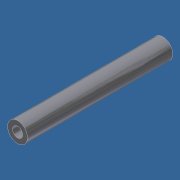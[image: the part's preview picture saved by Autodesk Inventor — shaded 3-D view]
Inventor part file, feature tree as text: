
AUTODESK INVENTOR PART (.ipt)
format: ipt  version: unknown  size: 171,520 bytes
history: native  units: in
note: dims shown in document units (in); Inventor stores cm internally (conversion verified against a paired STEP export)
features: extrude x3, sketch x3
ambient origin geometry x8: Origin, YZ Plane, XZ Plane, XY Plane, X Axis, Y Axis, Z Axis, Center Point
bodies: Solid1 (feature_tree)
feature tree (6):
  extrude  "Extrusion1"  Depth=1.806in TaperAngle=0.0deg
  extrude  "Extrusion2"  Depth=0.25in TaperAngle=0.0deg
  extrude  "Extrusion3"  Depth=0.25in TaperAngle=0.0deg
  sketch  "Sketch1"  dims[d0=0.249in d1=1.806in d2=0.0in]
  sketch  "Sketch2"  dims[d3=0.126in d4=0.25in d5=0.0in]
  sketch  "Sketch3"  dims[d6=0.126in d7=0.25in d8=0.0in]
